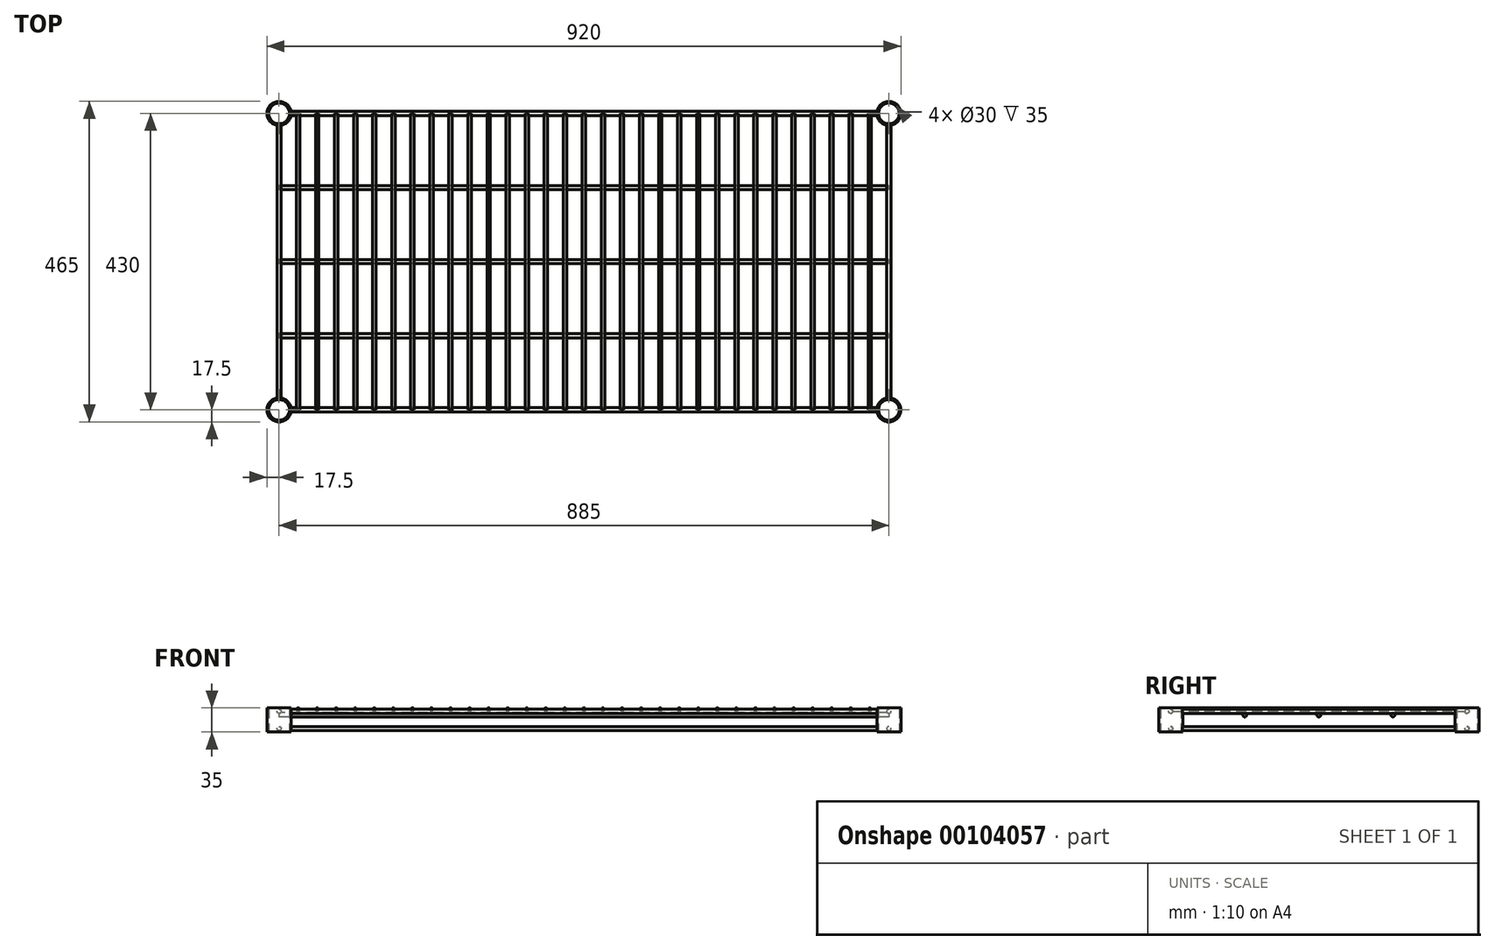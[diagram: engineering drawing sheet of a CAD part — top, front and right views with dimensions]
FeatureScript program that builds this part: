
annotation { "Feature Type Name" : "Feature", "Feature Type Description" : "" }
export const myFeature = defineFeature(function(context is Context, id is Id, definition is map)
    precondition{}
    {
        {
            var Q0;
            Q0=qCreatedBy(makeId("Front.planeOp"),FACE);
            cPlane(context, id + "F0", {"entities" : qUnion([Q0]), "cplaneType" : CPlaneType.OFFSET, "offset" : 430 * mm, "oppositeDirection" : true, "width" : 150 * mm, "height" : 150 * mm});
        }
        {
            var Q0;
            Q0=qCreatedBy(makeId("Right.planeOp"),FACE);
            cPlane(context, id + "F1", {"entities" : qUnion([Q0]), "cplaneType" : CPlaneType.OFFSET, "offset" : 885 * mm, "width" : 150 * mm, "height" : 150 * mm});
        }
        {
            var Q0;
            Q0=qCreatedBy(makeId("Top.planeOp"),FACE);
            var sketch = newSketch(context, id + "F2", { "sketchPlane" : qUnion([Q0])});
            skCircle(sketch, "E0", {"center": v(0, 0) * mm, "radius": 17.5 * mm});
            skCircle(sketch, "E1", {"center": v(0, 0) * mm, "radius": 15 * mm});
            skCircle(sketch, "E2", {"center": v(0, 430) * mm, "radius": 17.5 * mm});
            skCircle(sketch, "E3", {"center": v(0, 430) * mm, "radius": 15 * mm});
            skCircle(sketch, "E4", {"center": v(885, 0) * mm, "radius": 17.5 * mm});
            skCircle(sketch, "E5", {"center": v(885, 0) * mm, "radius": 15 * mm});
            skCircle(sketch, "E6", {"center": v(885, 430) * mm, "radius": 15 * mm});
            skCircle(sketch, "E7", {"center": v(885, 430) * mm, "radius": 17.5 * mm});
            skSolve(sketch);
        }
        {
            var Q0;
            Q0 = qSketchRegion(id + "F2", true);
            extrude(context, id + "F3", {"entities" : qUnion([Q0]), "depth" : 35 * mm});
        }
        {
            var Q0;
            Q0=qCreatedBy(makeId("Front.planeOp"),FACE);
            cPlane(context, id + "F4", {"entities" : qUnion([Q0]), "cplaneType" : CPlaneType.OFFSET, "offset" : 25 * mm, "oppositeDirection" : true, "width" : 150 * mm, "height" : 150 * mm});
        }
        {
            var Q0;
            Q0=qCreatedBy(makeId("Right.planeOp"),FACE);
            cPlane(context, id + "F5", {"entities" : qUnion([Q0]), "cplaneType" : CPlaneType.OFFSET, "offset" : 25 * mm, "width" : 150 * mm, "height" : 150 * mm});
        }
        {
            var Q0;
            Q0=qCreatedBy(id+"F4.planeOp",FACE);
            var sketch = newSketch(context, id + "F6", { "sketchPlane" : qUnion([Q0])});
            skCircle(sketch, "E8", {"center": v(0, 30) * mm, "radius": 3 * mm});
            skCircle(sketch, "E9", {"center": v(0, 5) * mm, "radius": 3 * mm});
            skCircle(sketch, "E10", {"center": v(885, 5) * mm, "radius": 3 * mm});
            skCircle(sketch, "E11", {"center": v(885, 30) * mm, "radius": 3 * mm});
            skSolve(sketch);
        }
        {
            var Q0;
            Q0 = qSketchRegion(id + "F6", true);
            extrude(context, id + "F7", {"entities" : qUnion([Q0]), "operationType" : NewBodyOperationType.ADD, "endBound" : BoundingType.UP_TO_NEXT, "depth" : 25 * mm, "hasSecondDirection" : true, "secondDirectionBound" : SecondDirectionBoundingType.UP_TO_NEXT, "secondDirectionOppositeDirection" : true, "secondDirectionDepth" : 25 * mm});
        }
        {
            var Q0;
            Q0=qCreatedBy(id+"F5.planeOp",FACE);
            var sketch = newSketch(context, id + "F8", { "sketchPlane" : qUnion([Q0])});
            skCircle(sketch, "E12", {"center": v(0, 5) * mm, "radius": 3 * mm});
            skCircle(sketch, "E13", {"center": v(0, 30) * mm, "radius": 3 * mm});
            skCircle(sketch, "E14", {"center": v(430, 5) * mm, "radius": 3 * mm});
            skCircle(sketch, "E15", {"center": v(430, 30) * mm, "radius": 3 * mm});
            skSolve(sketch);
        }
        {
            var Q0;
            Q0 = qSketchRegion(id + "F8", true);
            extrude(context, id + "F9", {"entities" : qUnion([Q0]), "operationType" : NewBodyOperationType.ADD, "endBound" : BoundingType.UP_TO_NEXT, "depth" : 25 * mm, "hasSecondDirection" : true, "secondDirectionBound" : SecondDirectionBoundingType.UP_TO_NEXT, "secondDirectionOppositeDirection" : true, "secondDirectionDepth" : 25 * mm});
        }
        {
            var Q0;
            Q0=qCreatedBy(makeId("Front.planeOp"),FACE);
            var Q1;
            Q1=qCreatedBy(id+"F0.planeOp",FACE);
            cPlane(context, id + "F10", {"entities" : qUnion([Q0, Q1]), "cplaneType" : CPlaneType.MID_PLANE, "offset" : 25 * mm, "width" : 150 * mm, "height" : 150 * mm});
        }
        {
            var Q0;
            Q0=qCreatedBy(makeId("Front.planeOp"),FACE);
            var Q1;
            Q1=qCreatedBy(id+"F10.planeOp",FACE);
            cPlane(context, id + "F11", {"entities" : qUnion([Q0, Q1]), "cplaneType" : CPlaneType.MID_PLANE, "offset" : 25 * mm, "width" : 150 * mm, "height" : 150 * mm});
        }
        {
            var Q0;
            Q0=qCreatedBy(id+"F10.planeOp",FACE);
            var Q1;
            Q1=qCreatedBy(id+"F0.planeOp",FACE);
            cPlane(context, id + "F12", {"entities" : qUnion([Q0, Q1]), "cplaneType" : CPlaneType.MID_PLANE, "offset" : 25 * mm, "width" : 150 * mm, "height" : 150 * mm});
        }
        {
            var Q0;
            Q0=qCreatedBy(makeId("Right.planeOp"),FACE);
            var sketch = newSketch(context, id + "F13", { "sketchPlane" : qUnion([Q0])});
            skCircle(sketch, "E16", {"center": v(215, 25) * mm, "radius": 3 * mm});
            skCircle(sketch, "E17", {"center": v(107.5, 25) * mm, "radius": 3 * mm});
            skCircle(sketch, "E18", {"center": v(322.5, 25) * mm, "radius": 3 * mm});
            skSolve(sketch);
        }
        {
            var Q0;
            Q0 = qSketchRegion(id + "F13", true);
            var Q1;
            Q1=qCreatedBy(id+"F1.planeOp",FACE);
            extrude(context, id + "F14", {"entities" : qUnion([Q0]), "operationType" : NewBodyOperationType.ADD, "endBound" : BoundingType.UP_TO_SURFACE, "endBoundEntityFace" : qUnion([Q1]), "depth" : 25 * mm});
        }
        {
            var Q0;
            Q0=qCreatedBy(id+"F1.planeOp",FACE);
            var Q1;
            Q1=qCreatedBy(makeId("Right.planeOp"),FACE);
            cPlane(context, id + "F15", {"entities" : qUnion([Q0, Q1]), "cplaneType" : CPlaneType.MID_PLANE, "offset" : 25 * mm, "width" : 150 * mm, "height" : 150 * mm});
        }
        {
            var Q0;
            Q0=qCreatedBy(makeId("Right.planeOp"),FACE);
            var Q1;
            Q1=qCreatedBy(id+"F15.planeOp",FACE);
            cPlane(context, id + "F16", {"entities" : qUnion([Q0, Q1]), "cplaneType" : CPlaneType.MID_PLANE, "offset" : 25 * mm, "width" : 150 * mm, "height" : 150 * mm});
        }
        {
            var Q0;
            Q0=qCreatedBy(makeId("Right.planeOp"),FACE);
            var Q1;
            Q1=qCreatedBy(id+"F16.planeOp",FACE);
            cPlane(context, id + "F17", {"entities" : qUnion([Q0, Q1]), "cplaneType" : CPlaneType.MID_PLANE, "offset" : 25 * mm, "width" : 150 * mm, "height" : 150 * mm});
        }
        {
            var Q0;
            Q0=qCreatedBy(id+"F16.planeOp",FACE);
            var Q1;
            Q1=qCreatedBy(id+"F15.planeOp",FACE);
            cPlane(context, id + "F18", {"entities" : qUnion([Q0, Q1]), "cplaneType" : CPlaneType.MID_PLANE, "offset" : 25 * mm, "width" : 150 * mm, "height" : 150 * mm});
        }
        {
            var Q0;
            Q0=qCreatedBy(makeId("Right.planeOp"),FACE);
            var Q1;
            Q1=qCreatedBy(id+"F17.planeOp",FACE);
            cPlane(context, id + "F19", {"entities" : qUnion([Q0, Q1]), "cplaneType" : CPlaneType.MID_PLANE, "offset" : 25 * mm, "width" : 150 * mm, "height" : 150 * mm});
        }
        {
            var Q0;
            Q0=qCreatedBy(id+"F17.planeOp",FACE);
            var Q1;
            Q1=qCreatedBy(id+"F16.planeOp",FACE);
            cPlane(context, id + "F20", {"entities" : qUnion([Q0, Q1]), "cplaneType" : CPlaneType.MID_PLANE, "offset" : 25 * mm, "width" : 150 * mm, "height" : 150 * mm});
        }
        {
            var Q0;
            Q0=qCreatedBy(id+"F16.planeOp",FACE);
            var Q1;
            Q1=qCreatedBy(id+"F18.planeOp",FACE);
            cPlane(context, id + "F21", {"entities" : qUnion([Q0, Q1]), "cplaneType" : CPlaneType.MID_PLANE, "offset" : 25 * mm, "width" : 150 * mm, "height" : 150 * mm});
        }
        {
            var Q0;
            Q0=qCreatedBy(id+"F18.planeOp",FACE);
            var Q1;
            Q1=qCreatedBy(id+"F15.planeOp",FACE);
            cPlane(context, id + "F22", {"entities" : qUnion([Q0, Q1]), "cplaneType" : CPlaneType.MID_PLANE, "offset" : 25 * mm, "width" : 150 * mm, "height" : 150 * mm});
        }
        {
            var Q0;
            Q0=qCreatedBy(makeId("Right.planeOp"),FACE);
            var Q1;
            Q1=qCreatedBy(id+"F19.planeOp",FACE);
            cPlane(context, id + "F23", {"entities" : qUnion([Q0, Q1]), "cplaneType" : CPlaneType.MID_PLANE, "offset" : 25 * mm, "width" : 150 * mm, "height" : 150 * mm});
        }
        {
            var Q0;
            Q0=qCreatedBy(id+"F19.planeOp",FACE);
            var Q1;
            Q1=qCreatedBy(id+"F17.planeOp",FACE);
            cPlane(context, id + "F24", {"entities" : qUnion([Q0, Q1]), "cplaneType" : CPlaneType.MID_PLANE, "offset" : 25 * mm, "width" : 150 * mm, "height" : 150 * mm});
        }
        {
            var Q0;
            Q0=qCreatedBy(id+"F17.planeOp",FACE);
            var Q1;
            Q1=qCreatedBy(id+"F20.planeOp",FACE);
            cPlane(context, id + "F25", {"entities" : qUnion([Q0, Q1]), "cplaneType" : CPlaneType.MID_PLANE, "offset" : 25 * mm, "width" : 150 * mm, "height" : 150 * mm});
        }
        {
            var Q0;
            Q0=qCreatedBy(id+"F20.planeOp",FACE);
            var Q1;
            Q1=qCreatedBy(id+"F16.planeOp",FACE);
            cPlane(context, id + "F26", {"entities" : qUnion([Q0, Q1]), "cplaneType" : CPlaneType.MID_PLANE, "offset" : 25 * mm, "width" : 150 * mm, "height" : 150 * mm});
        }
        {
            var Q0;
            Q0=qCreatedBy(id+"F16.planeOp",FACE);
            var Q1;
            Q1=qCreatedBy(id+"F21.planeOp",FACE);
            cPlane(context, id + "F27", {"entities" : qUnion([Q0, Q1]), "cplaneType" : CPlaneType.MID_PLANE, "offset" : 25 * mm, "width" : 150 * mm, "height" : 150 * mm});
        }
        {
            var Q0;
            Q0=qCreatedBy(id+"F21.planeOp",FACE);
            var Q1;
            Q1=qCreatedBy(id+"F18.planeOp",FACE);
            cPlane(context, id + "F28", {"entities" : qUnion([Q0, Q1]), "cplaneType" : CPlaneType.MID_PLANE, "offset" : 25 * mm, "width" : 150 * mm, "height" : 150 * mm});
        }
        {
            var Q0;
            Q0=qCreatedBy(id+"F18.planeOp",FACE);
            var Q1;
            Q1=qCreatedBy(id+"F22.planeOp",FACE);
            cPlane(context, id + "F29", {"entities" : qUnion([Q0, Q1]), "cplaneType" : CPlaneType.MID_PLANE, "offset" : 25 * mm, "width" : 150 * mm, "height" : 150 * mm});
        }
        {
            var Q0;
            Q0=qCreatedBy(id+"F22.planeOp",FACE);
            var Q1;
            Q1=qCreatedBy(id+"F15.planeOp",FACE);
            cPlane(context, id + "F30", {"entities" : qUnion([Q0, Q1]), "cplaneType" : CPlaneType.MID_PLANE, "offset" : 25 * mm, "width" : 150 * mm, "height" : 150 * mm});
        }
        {
            var Q0;
            Q0=qCreatedBy(id+"F4.planeOp",FACE);
            var sketch = newSketch(context, id + "F31", { "sketchPlane" : qUnion([Q0])});
            skCircle(sketch, "E19", {"center": v(27.66, 32.5) * mm, "radius": 2.5 * mm});
            skCircle(sketch, "E20", {"center": v(55.31, 32.5) * mm, "radius": 2.5 * mm});
            skCircle(sketch, "E21", {"center": v(82.97, 32.5) * mm, "radius": 2.5 * mm});
            skCircle(sketch, "E22", {"center": v(110.62, 32.5) * mm, "radius": 2.5 * mm});
            skCircle(sketch, "E23", {"center": v(138.28, 32.5) * mm, "radius": 2.5 * mm});
            skCircle(sketch, "E24", {"center": v(165.94, 32.5) * mm, "radius": 2.5 * mm});
            skCircle(sketch, "E25", {"center": v(193.6, 32.5) * mm, "radius": 2.5 * mm});
            skCircle(sketch, "E26", {"center": v(221.25, 32.5) * mm, "radius": 2.5 * mm});
            skCircle(sketch, "E27", {"center": v(248.9, 32.5) * mm, "radius": 2.5 * mm});
            skCircle(sketch, "E28", {"center": v(276.56, 32.5) * mm, "radius": 2.5 * mm});
            skCircle(sketch, "E29", {"center": v(304.22, 32.5) * mm, "radius": 2.5 * mm});
            skCircle(sketch, "E30", {"center": v(331.88, 32.5) * mm, "radius": 2.5 * mm});
            skCircle(sketch, "E31", {"center": v(359.53, 32.5) * mm, "radius": 2.5 * mm});
            skCircle(sketch, "E32", {"center": v(387.19, 32.5) * mm, "radius": 2.5 * mm});
            skCircle(sketch, "E33", {"center": v(414.84, 32.5) * mm, "radius": 2.5 * mm});
            skCircle(sketch, "E34", {"center": v(442.5, 32.5) * mm, "radius": 2.5 * mm});
            skCircle(sketch, "E35.MirrorC", {"center": v(802.03, 32.5) * mm, "radius": 2.5 * mm});
            skCircle(sketch, "E36.MirrorC", {"center": v(774.38, 32.5) * mm, "radius": 2.5 * mm});
            skCircle(sketch, "E37.MirrorC", {"center": v(746.72, 32.5) * mm, "radius": 2.5 * mm});
            skCircle(sketch, "E38.MirrorC", {"center": v(719.06, 32.5) * mm, "radius": 2.5 * mm});
            skCircle(sketch, "E39.MirrorC", {"center": v(691.4, 32.5) * mm, "radius": 2.5 * mm});
            skCircle(sketch, "E40.MirrorC", {"center": v(663.75, 32.5) * mm, "radius": 2.5 * mm});
            skCircle(sketch, "E41.MirrorC", {"center": v(636.1, 32.5) * mm, "radius": 2.5 * mm});
            skCircle(sketch, "E42.MirrorC", {"center": v(608.44, 32.5) * mm, "radius": 2.5 * mm});
            skCircle(sketch, "E43.MirrorC", {"center": v(580.78, 32.5) * mm, "radius": 2.5 * mm});
            skCircle(sketch, "E44.MirrorC", {"center": v(553.12, 32.5) * mm, "radius": 2.5 * mm});
            skCircle(sketch, "E45.MirrorC", {"center": v(525.47, 32.5) * mm, "radius": 2.5 * mm});
            skCircle(sketch, "E46.MirrorC", {"center": v(829.69, 32.5) * mm, "radius": 2.5 * mm});
            skCircle(sketch, "E47.MirrorC", {"center": v(857.34, 32.5) * mm, "radius": 2.5 * mm});
            skCircle(sketch, "E48.MirrorC", {"center": v(470.16, 32.5) * mm, "radius": 2.5 * mm});
            skCircle(sketch, "E49.MirrorC", {"center": v(497.81, 32.5) * mm, "radius": 2.5 * mm});
            skSolve(sketch);
        }
        {
            var Q0;
            Q0 = qSketchRegion(id + "F31", true);
            var Q1;
            Q1=qCreatedBy(makeId("Front.planeOp"),FACE);
            var Q2;
            Q2=makeQuery(id+"F3.opExtrude","SWEPT_BODY",BODY,{"disambiguationData":[OSD([sQuery(id+"F2.wireOp",EDGE,"E0"),sQuery(id+"F2.wireOp",EDGE,"E1")])]});
            var Q3;
            Q3=qCreatedBy(id+"F0.planeOp",FACE);
            extrude(context, id + "F32", {"entities" : qUnion([Q0]), "operationType" : NewBodyOperationType.ADD, "endBound" : BoundingType.UP_TO_SURFACE, "endBoundEntityFace" : qUnion([Q1]), "endBoundEntityBody" : qUnion([Q2]), "depth" : 25 * mm, "hasSecondDirection" : true, "secondDirectionBound" : SecondDirectionBoundingType.UP_TO_SURFACE, "secondDirectionOppositeDirection" : true, "secondDirectionBoundEntityFace" : qUnion([Q3]), "secondDirectionDepth" : 25 * mm});
        }
    });
